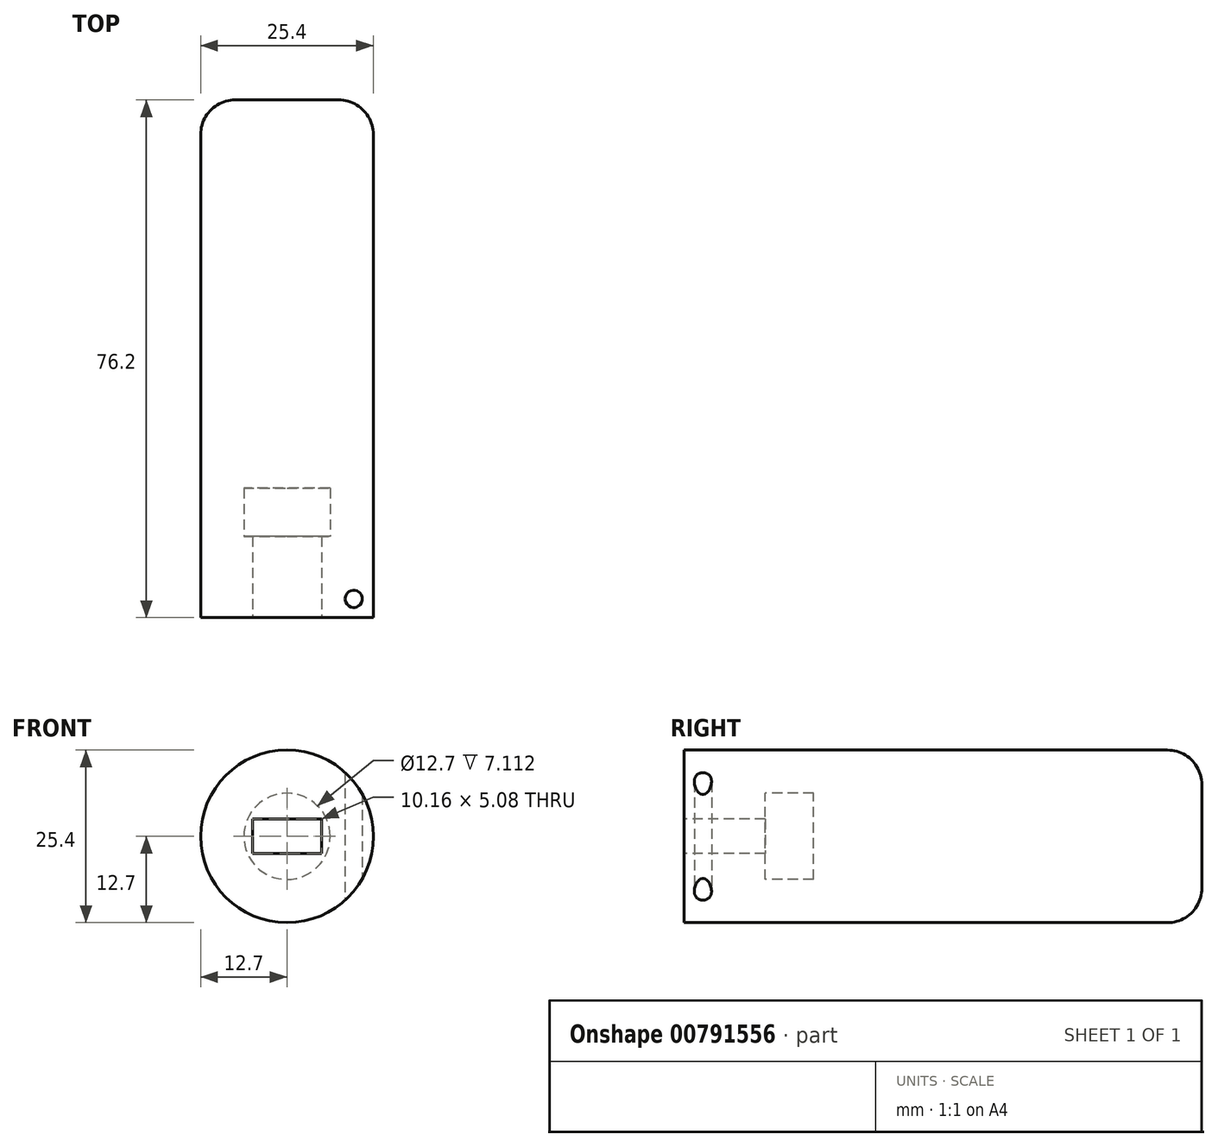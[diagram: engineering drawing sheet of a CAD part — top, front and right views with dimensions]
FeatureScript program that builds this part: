
annotation { "Feature Type Name" : "Feature", "Feature Type Description" : "" }
export const myFeature = defineFeature(function(context is Context, id is Id, definition is map)
    precondition{}
    {
        {
            var Q0;
            Q0=qCreatedBy(makeId("Front.planeOp"),FACE);
            var sketch = newSketch(context, id + "F0", { "sketchPlane" : qUnion([Q0])});
            skCircle(sketch, "E0", {"center": v(0, 0) * mm, "radius": 12.7 * mm});
            skSolve(sketch);
        }
        {
            var Q0;
            Q0 = qSketchRegion(id + "F0", true);
            extrude(context, id + "F1", {"entities" : qUnion([Q0]), "oppositeDirection" : true, "depth" : 76.2 * mm, "offsetDistance" : 25.4 * mm});
        }
        {
            var Q0;
            Q0=makeQuery(id+"F1.opExtrude","CAP_FACE",FACE,{"disambiguationData":[OSD([sQuery(id+"F0.wireOp",EDGE,"E0")])],"isStart":true});
            var sketch = newSketch(context, id + "F2", { "sketchPlane" : qUnion([Q0])});
            skLineSegment(sketch, "E1", {"start": v(5.08, 0) * mm, "end": v(5.08, -2.54) * mm});
            skLineSegment(sketch, "E2", {"start": v(5.08, -2.54) * mm, "end": v(5.08, 2.54) * mm});
            skLineSegment(sketch, "E3", {"start": v(5.08, 2.54) * mm, "end": v(-5.08, 2.54) * mm});
            skLineSegment(sketch, "E4", {"start": v(-5.08, 2.54) * mm, "end": v(-5.08, -2.54) * mm});
            skLineSegment(sketch, "E5", {"start": v(-5.08, -2.54) * mm, "end": v(5.08, -2.54) * mm});
            skSolve(sketch);
        }
        {
            var Q0;
            {var subQ0=sQuery(id+"F2.wireOp",EDGE,"E3");Q0=makeQuery(id+"F2.imprint","IMPRINT",FACE,{"disambiguationData":[TD([[makeQuery(id+"F2.imprint","IMPRINT",EDGE,{"derivedFrom":subQ0}),-1.0]])]});}
            var sketch = newSketch(context, id + "F3", { "sketchPlane" : qUnion([Q0])});
            skCircle(sketch, "E6", {"center": v(0, 0) * mm, "radius": 6.35 * mm});
            skSolve(sketch);
        }
        {
            var Q0;
            Q0 = qSketchRegion(id + "F3", true);
            extrude(context, id + "F4", {"entities" : qUnion([Q0]), "operationType" : NewBodyOperationType.REMOVE, "oppositeDirection" : true, "depth" : 19.05 * mm, "offsetDistance" : 25.4 * mm});
        }
        {
            var Q0;
            {var subQ0=sQuery(id+"F2.wireOp",EDGE,"E3");Q0=makeQuery(id+"F2.imprint","IMPRINT",FACE,{"disambiguationData":[TD([[makeQuery(id+"F2.imprint","IMPRINT",EDGE,{"derivedFrom":subQ0}),1.0]])]});}
            var sketch = newSketch(context, id + "F5", { "sketchPlane" : qUnion([Q0])});
            skCircle(sketch, "E7", {"center": v(0, 0) * mm, "radius": 6.35 * mm});
            skSolve(sketch);
        }
        {
            var Q0;
            Q0 = qSketchRegion(id + "F5", true);
            extrude(context, id + "F6", {"entities" : qUnion([Q0]), "operationType" : NewBodyOperationType.ADD, "oppositeDirection" : true, "depth" : 11.94 * mm, "offsetDistance" : 25.4 * mm});
        }
        {
            var Q0;
            Q0 = qSketchRegion(id + "F2", true);
            extrude(context, id + "F7", {"entities" : qUnion([Q0]), "operationType" : NewBodyOperationType.REMOVE, "oppositeDirection" : true, "depth" : 19.05 * mm, "offsetDistance" : 25.4 * mm});
        }
        {
            var Q0;
            Q0=makeQuery(id+"F1.opExtrude","CAP_EDGE",EDGE,{"disambiguationData":[OSD([sQuery(id+"F0.wireOp",EDGE,"E0")])],"isStart":false});
            fillet(context, id + "F8", {"entities" : qUnion([Q0]), "radius" : 5.08 * mm, "tangentPropagation" : true, "allowEdgeOverflow" : false});
        }
        {
            var Q0;
            Q0=qCreatedBy(makeId("Top.planeOp"),FACE);
            var sketch = newSketch(context, id + "F9", { "sketchPlane" : qUnion([Q0])});
            skCircle(sketch, "E8", {"center": v(9.82, 2.76) * mm, "radius": 1.27 * mm});
            skSolve(sketch);
        }
        {
            var Q0;
            Q0 = qSketchRegion(id + "F9", true);
            extrude(context, id + "F10", {"entities" : qUnion([Q0]), "operationType" : NewBodyOperationType.REMOVE, "depth" : 25.4 * mm, "offsetDistance" : 25.4 * mm, "hasSecondDirection" : true, "secondDirectionOppositeDirection" : true, "secondDirectionDepth" : 25.4 * mm});
        }
    });
